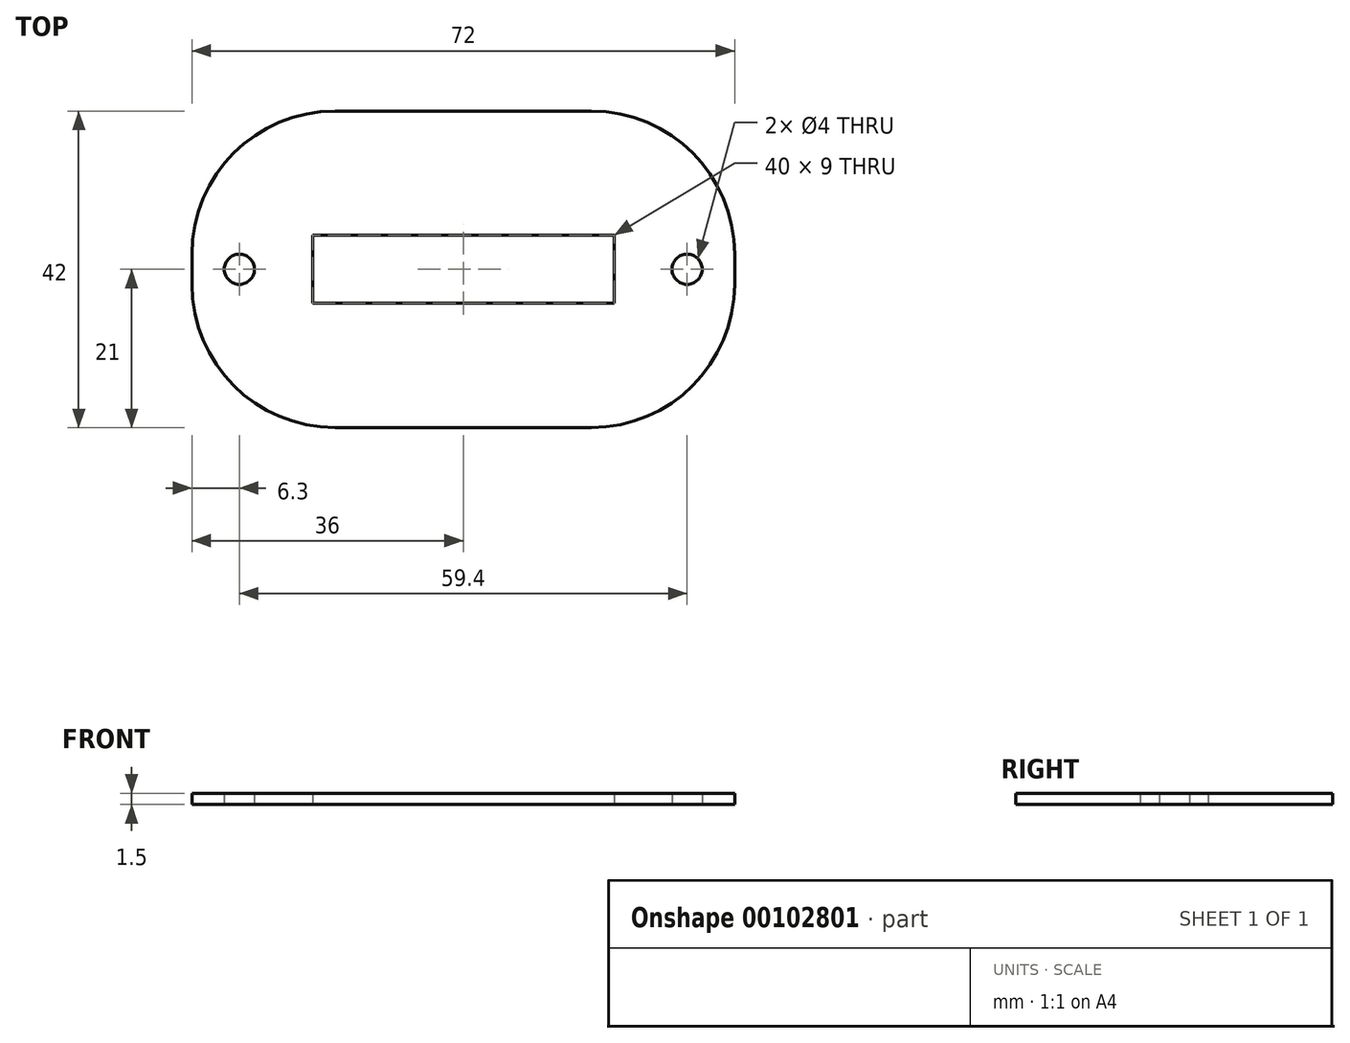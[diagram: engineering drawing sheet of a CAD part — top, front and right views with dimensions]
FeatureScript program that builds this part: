
annotation { "Feature Type Name" : "Feature", "Feature Type Description" : "" }
export const myFeature = defineFeature(function(context is Context, id is Id, definition is map)
    precondition{}
    {
        {
            var Q0;
            Q0=qCreatedBy(makeId("Top.planeOp"),FACE);
            var sketch = newSketch(context, id + "F0", { "sketchPlane" : qUnion([Q0])});
            skLineSegment(sketch, "E0.bottom", {"start": v(20, -4.5) * mm, "end": v(-20, -4.5) * mm});
            skLineSegment(sketch, "E0.top", {"start": v(20, 4.5) * mm, "end": v(-20, 4.5) * mm});
            skLineSegment(sketch, "E0.left", {"start": v(20, -4.5) * mm, "end": v(20, 4.5) * mm});
            skLineSegment(sketch, "E0.right", {"start": v(-20, -4.5) * mm, "end": v(-20, 4.5) * mm});
            skPoint(sketch, "E0.middle", {"position": v(0, 0) * mm});
            skLineSegment(sketch, "E1.bottom", {"start": v(17, -21) * mm, "end": v(-17, -21) * mm});
            skLineSegment(sketch, "E1.top", {"start": v(17, 21) * mm, "end": v(-17, 21) * mm});
            skLineSegment(sketch, "E1.left", {"start": v(36, -2) * mm, "end": v(36, 2) * mm});
            skLineSegment(sketch, "E1.right", {"start": v(-36, -2) * mm, "end": v(-36, 2) * mm});
            skCircle(sketch, "E2", {"center": v(-29.7, 0) * mm, "radius": 2 * mm});
            skCircle(sketch, "E3.MirrorC", {"center": v(29.7, 0) * mm, "radius": 2 * mm});
            skPoint(sketch, "E4.visualSharp", {"position": v(-36, 21) * mm});
            skArc(sketch, "E4.filletArc", {"start": v(-17, 21) * mm, "mid": v(-30.44, 15.44) * mm, "end": v(-36, 2) * mm});
            skPoint(sketch, "E5.visualSharp", {"position": v(-36, -21) * mm});
            skArc(sketch, "E5.filletArc", {"start": v(-36, -2) * mm, "mid": v(-30.44, -15.44) * mm, "end": v(-17, -21) * mm});
            skPoint(sketch, "E6.visualSharp", {"position": v(36, -21) * mm});
            skArc(sketch, "E6.filletArc", {"start": v(17, -21) * mm, "mid": v(30.44, -15.44) * mm, "end": v(36, -2) * mm});
            skPoint(sketch, "E7.visualSharp", {"position": v(36, 21) * mm});
            skArc(sketch, "E7.filletArc", {"start": v(36, 2) * mm, "mid": v(30.44, 15.44) * mm, "end": v(17, 21) * mm});
            skSolve(sketch);
        }
        {
            var Q0;
            Q0 = qSketchRegion(id + "F0", true);
            extrude(context, id + "F1", {"entities" : qUnion([Q0]), "depth" : 1.5 * mm});
        }
    });
